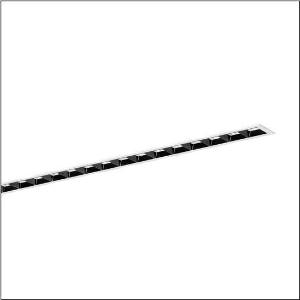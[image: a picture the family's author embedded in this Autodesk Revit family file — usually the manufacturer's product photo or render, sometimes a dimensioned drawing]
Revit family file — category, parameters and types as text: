
# Revit family: silica_21_51mx12db45wb
name_source: partatom
category: Lighting Fixtures
units: mm (PartAtom-declared; Revit-internal decimal feet)

## family parameters
Cut with Voids When Loaded = No
Host = Face
Light Source = No
Part Type = Normal
Room Calculation Point = No
Round Connector Dimension = Use Diameter
Shared = No

## types (1)
- --- (1 x LED, 5400 lm, 32 W, 4000K)
    Apparent Load = 32 VA
    CIE Flux Codes = 86 100 100 100 100
    Color Rendering = 80
    Color Temperature = 4000K
    Default Elevation = 1800 mm
    Description = Silica 21, office luminaire, primary light control with darklight reflector, of PMMA, black, CAT 2 (L<= 3000cd/m²), light emission: direct distribution, primary light characteristic: symmetric, installation type: recessed, LED, rated luminous flux: 5.400lm, luminous efficacy: 169lm/W, light colour: 840, colour temperature: 4000K, control gear: DALI 2, with terminal, 3+2-pole, max. 2.5mm², mains connection: 220..240V, AC, 50/60Hz, rated input power: 32W, luminaire housing, of aluminium, traffic white (RAL 9016), length: 1.528mm, width: 79mm, height: 53mm, protection rating (complete): IP20, insulation class (complete): insulation class I (protective earthing), certification: CE, ENEC, VDE, permissible operating ambient temperature: 0..+35°C, standard: EN 50419, packaging unit: 1 piece
    Height = 0 mm  [stored 0 ft]
    Lamp = 1 x LED
    Lamp Light Flux = 5400 lm
    Lamp Power = 32 W
    Lamp count = 1
    Length = 1527 mm
    Luminous efficacy = 169 lm/W
    Manufacturer = Siteco
    ModVariant = No
    Model = 51MX12DB45WB
    Mounting Place = Ceiling
    Mounting Type = Recessed
    Number of Poles = 1
    OnlyDefault = Yes
    Power Factor = 1
    Product Name = Silica 21
    Product group = office luminaire | ceiling recessed
    ProductGroupID = 400
    Protection Class = Protection class I
    Protection Degree = IP 20
    RLX_Detail_Level = 1
    RLX_Emergency_Light_Flux = 0 lm
    RLX_Emergency_Type = 0
    RLX_Emergency_Type_DB = No
    RlxData = <blob elided: 42361 chars, md5=5a628f10>
    Socket = socket
    Standby Power = 0 W
    System Light Flux = 5400 lm
    System Power = 32 W
    Type Comments = factory setting: luminous flux: 100 % | dim-lin: 254 | 366 mA
    Type Image = l_1335880.jpg
    URL = http://relux.com
    VarID = @adj_126185
    Voltage = 0 V
    Weight = 0.00 kg
    Width = 79 mm

note: [stored X ft] marks values corroborated as IEEE doubles in the binary element streams (Revit-internal decimal feet)

## geometry (parser evidence)
native form markers: Blend x4, Sweep x10
no freeform markers — native parametric forms only
